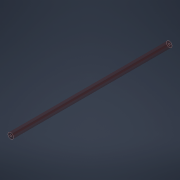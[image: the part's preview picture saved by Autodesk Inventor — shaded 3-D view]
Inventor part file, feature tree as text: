
AUTODESK INVENTOR PART (.ipt)
format: ipt  version: 2022 (Build 260153000, 153)  size: 110,592 bytes
history: native  units: mm
features: extrude x2, sketch x2
ambient origin geometry x8: Origin, YZ Plane, XZ Plane, XY Plane, X Axis, Y Axis, Z Axis, Center Point
bodies: Solid1 (feature_tree)
feature tree (4):
  extrude  "Extrusion1"  TaperAngle=0.0deg  [1 undecoded]
  extrude  "Extrusion2"  [1 undecoded]
  sketch  "Sketch1"  dims[d0=4200.0mm d1=0.0mm d2=0.0mm d3=0.0mm]
  sketch  "Sketch2"
note: 2 required parameter values undecoded (feature->parameter linkage not recoverable at this tier; creation-order binding heuristic only, values carry confidence <= 0.55)
